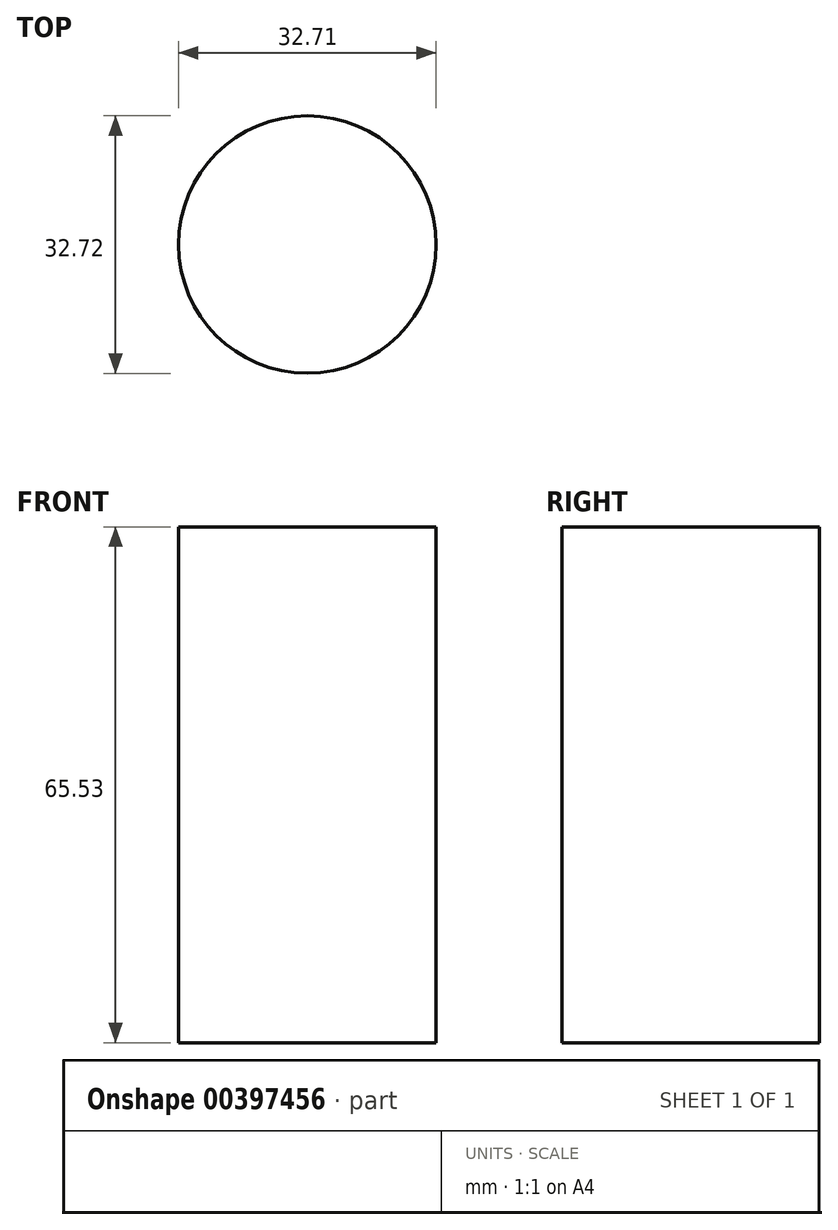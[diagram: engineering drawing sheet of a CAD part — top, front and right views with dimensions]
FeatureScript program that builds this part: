
annotation { "Feature Type Name" : "Feature", "Feature Type Description" : "" }
export const myFeature = defineFeature(function(context is Context, id is Id, definition is map)
    precondition{}
    {
        {
            var Q0;
            Q0=qCreatedBy(makeId("Top.planeOp"),FACE);
            var sketch = newSketch(context, id + "F0", { "sketchPlane" : qUnion([Q0])});
            skCircle(sketch, "E0", {"center": v(-40.7, 37.03) * mm, "radius": 16.36 * mm});
            skSolve(sketch);
        }
        {
            var Q0;
            Q0=makeQuery(id+"F0.imprint","IMPRINT",FACE,{"disambiguationData":[TD([[makeQuery(id+"F0.imprint","IMPRINT",EDGE,{"derivedFrom":sQuery(id+"F0.wireOp",EDGE,"E0")}),1.0]])]});
            extrude(context, id + "F1", {"entities" : qUnion([Q0]), "depth" : 65.53 * mm});
        }
    });
